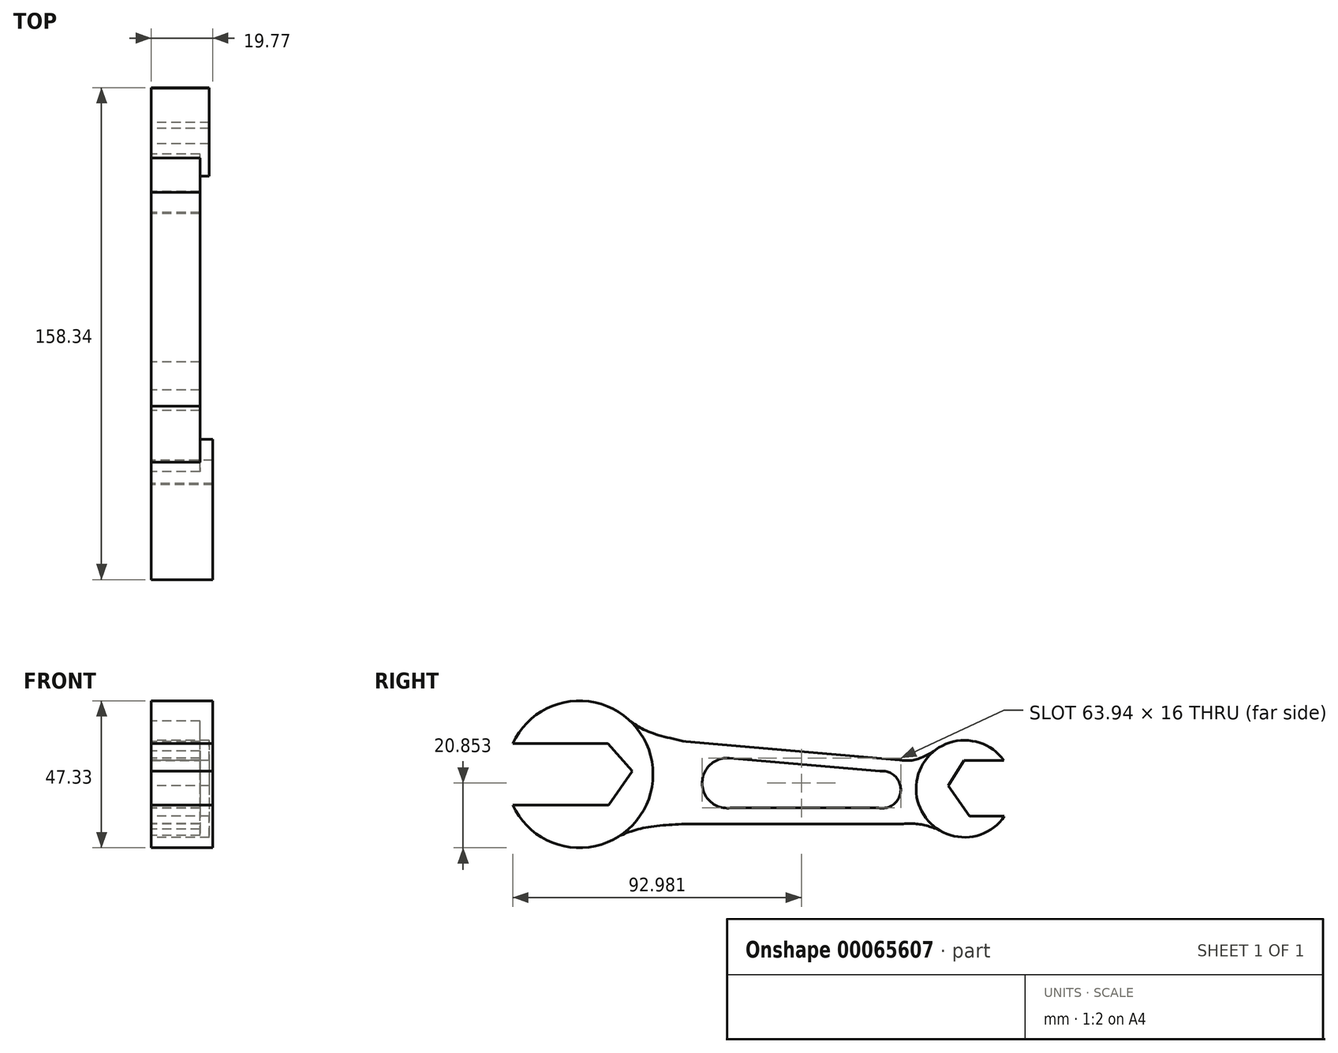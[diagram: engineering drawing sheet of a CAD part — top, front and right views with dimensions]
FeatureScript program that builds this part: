
annotation { "Feature Type Name" : "Feature", "Feature Type Description" : "" }
export const myFeature = defineFeature(function(context is Context, id is Id, definition is map)
    precondition{}
    {
        {
            var Q0;
            Q0=qCreatedBy(makeId("Right.planeOp"),FACE);
            var sketch = newSketch(context, id + "F0", { "sketchPlane" : qUnion([Q0])});
            skPoint(sketch, "E0.1.internal.snap0", {"position": v(-15.52, 5.78) * mm});
            skPoint(sketch, "E0.2.internal.snap0", {"position": v(-15.52, 5.78) * mm});
            skLineSegment(sketch, "E1", {"start": v(98.8, 3.4) * mm, "end": v(85.89, 3.4) * mm});
            skLineSegment(sketch, "E2", {"start": v(85.89, 3.4) * mm, "end": v(80.86, -4.64) * mm});
            skLineSegment(sketch, "E3", {"start": v(80.86, -4.64) * mm, "end": v(87.73, -14.53) * mm});
            skLineSegment(sketch, "E4", {"start": v(87.73, -14.53) * mm, "end": v(98.96, -14.53) * mm});
            skArc(sketch, "E5", {"start": v(98.8, 3.4) * mm, "mid": v(70.51, -5.82) * mm, "end": v(98.96, -14.53) * mm});
            skFitSpline(sketch, "E6", {"points": [v(65.27, 3.57) * mm, v(69.8, 3.57) * mm, v(76.33, 6.47) * mm], "startDerivative": vector(9.87, -1.15) * mm, "endDerivative": vector(12.17, 6.63) * mm});
            skFitSpline(sketch, "E7", {"points": [v(65.27, -17.04) * mm, v(71.3, -17.04) * mm, v(77.55, -18.72) * mm], "startDerivative": vector(12.28, 0.82) * mm, "endDerivative": vector(12.25, -4.17) * mm});
            skLineSegment(sketch, "E8", {"start": v(65.27, 3.57) * mm, "end": v(-3.58, 9.5) * mm});
            skLineSegment(sketch, "E9", {"start": v(65.27, -17.04) * mm, "end": v(-5, -17.04) * mm});
            skArc(sketch, "E10", {"start": v(58.42, -11.83) * mm, "mid": v(65.57, -6.16) * mm, "end": v(58.84, 0) * mm});
            skLineSegment(sketch, "E11", {"start": v(58.84, 0) * mm, "end": v(10.37, 4.17) * mm});
            skLineSegment(sketch, "E12", {"start": v(58.42, -11.83) * mm, "end": v(10.7, -11.83) * mm});
            skArc(sketch, "E13", {"start": v(10.37, 4.17) * mm, "mid": v(1.63, -4.01) * mm, "end": v(10.7, -11.83) * mm});
            skLineSegment(sketch, "E14", {"start": v(-59.38, 8.84) * mm, "end": v(-28.78, 8.84) * mm});
            skLineSegment(sketch, "E15", {"start": v(-28.78, 8.84) * mm, "end": v(-20.93, 0) * mm});
            skLineSegment(sketch, "E16", {"start": v(-20.93, 0) * mm, "end": v(-28.5, -10.87) * mm});
            skLineSegment(sketch, "E17", {"start": v(-28.5, -10.87) * mm, "end": v(-59.38, -10.87) * mm});
            skArc(sketch, "E18", {"start": v(-59.38, -10.87) * mm, "mid": v(-14.21, -1.01) * mm, "end": v(-59.38, 8.84) * mm});
            skFitSpline(sketch, "E19", {"points": [v(-3.58, 9.5) * mm, v(-16.05, 12.86) * mm, v(-21.63, 16.2) * mm], "startDerivative": vector(-23.61, 5.1) * mm, "endDerivative": vector(-11.86, 8.45) * mm});
            skFitSpline(sketch, "E20", {"points": [v(-5, -17.04) * mm, v(-17.2, -18.26) * mm, v(-24.66, -20.64) * mm], "startDerivative": vector(-23.38, -1.33) * mm, "endDerivative": vector(-15.65, -6.03) * mm});
            skSolve(sketch);
        }
        {
            var Q0;
            {var subQ1=sQuery(id+"F0.wireOp",EDGE,"E14");Q0=makeQuery(id+"F0.imprint","IMPRINT",FACE,{"disambiguationData":[TD([[makeQuery(id+"F0.imprint","IMPRINT",EDGE,{"derivedFrom":subQ1}),1.0]])]});}
            extrude(context, id + "F1", {"entities" : qUnion([Q0]), "depth" : 19.77 * mm});
        }
        {
            var Q0;
            {var subQ3=sQuery(id+"F0.wireOp",EDGE,"E6");Q0=makeQuery(id+"F0.imprint","IMPRINT",FACE,{"disambiguationData":[TD([[makeQuery(id+"F0.imprint","IMPRINT",EDGE,{"derivedFrom":subQ3}),-1.0]])]});}
            extrude(context, id + "F2", {"entities" : qUnion([Q0]), "operationType" : NewBodyOperationType.ADD, "depth" : 15.7 * mm});
        }
        {
            var Q0;
            {var subQ1=sQuery(id+"F0.wireOp",EDGE,"E1");Q0=makeQuery(id+"F0.imprint","IMPRINT",FACE,{"disambiguationData":[TD([[makeQuery(id+"F0.imprint","IMPRINT",EDGE,{"derivedFrom":subQ1}),-1.0]])]});}
            extrude(context, id + "F3", {"entities" : qUnion([Q0]), "operationType" : NewBodyOperationType.ADD, "depth" : 18.63 * mm});
        }
    });
